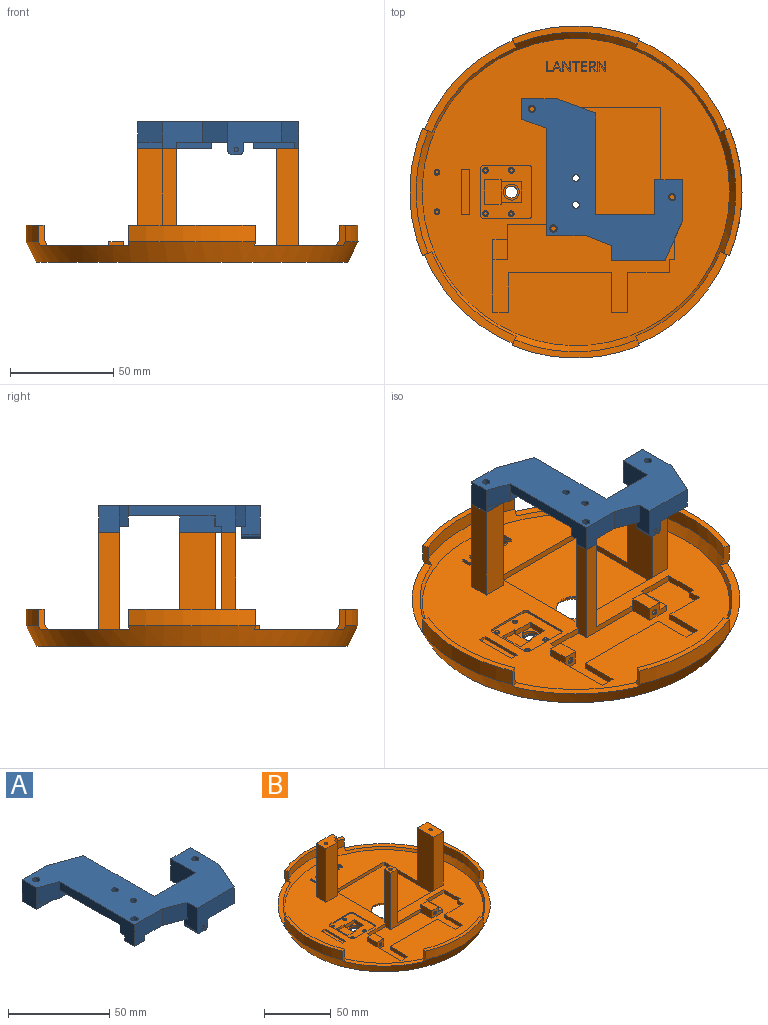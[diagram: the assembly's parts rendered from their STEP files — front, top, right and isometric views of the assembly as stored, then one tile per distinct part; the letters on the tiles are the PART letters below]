
ASSEMBLY  parts=2 mates=1
PART A: 45 faces, bbox 78x78.3x16 mm
  f0: plane 64.21x22mm, normal (0,0,-1), area 784.3mm2, adj f2,f4,f9,f10,f11,f16,f24,f27
  f1: plane 49.3x10mm, normal (1,0,0), area 283.3mm2, adj f2,f18,f23,f33,f35,f36
  f2: plane 28.5x10mm, normal (0,1,0), area 280mm2, adj f0,f1,f24,f33,f35,f38
  f3: plane 2x2mm, normal (0,-1,0), area 3.1mm2, adj f14
  f4: plane 4x3mm, normal (-1,0,0), area 12mm2, adj f0,f9,f10,f17
  f5: plane 3x3mm, normal (1,0,0), area 9mm2, adj f6,f7,f8,f18
  f6: plane 12x3mm, normal (0,-1,0), area 36mm2, adj f5,f7,f18,f21
  f7: plane 36x10mm, normal (0,0,-1), area 210.5mm2, adj f5,f6,f8,f19,f21,f22,f23
  f8: plane 24x3mm, normal (0,-1,0), area 72mm2, adj f5,f7,f18,f23
  f9: plane 8.26x3mm, normal (0,1,0), area 24.8mm2, adj f0,f4,f17,f24
  f10: plane 19.97x3mm, normal (0,-1,0), area 59.9mm2, adj f0,f4,f17,f27
  f11: plane 9x4mm, normal (1,0,0), area 36mm2, adj f0,f12,f16,f28
  f12: cylinder r=2mm len=9mm, axis (0,1,0), area 28.3mm2, adj f11,f13,f16,f28
  f13: plane 9x3.5mm, normal (0,0,-1), area 31.5mm2, adj f12,f15,f16,f28
  f14: cylinder r=1mm len=6mm, axis (0,-1,0), area 37.7mm2, adj f3,f28
  f15: cylinder r=2mm len=9mm, axis (0,-1,0), area 28.3mm2, adj f13,f16,f28,f29
  f16: plane 7.5x6mm, normal (0,1,0), area 43.3mm2, adj f0,f11,f12,f13,f15,f29
  f17: plane 24x21.76mm, normal (0,0,-1), area 343.3mm2, adj f4,f9,f10,f24,f25,f26,f27,f32
  f18: plane 36x7.37mm, normal (0,0,-1), area 203mm2, adj f1,f5,f6,f8,f20,f36
  f19: cylinder r=1.8mm len=13mm, axis (0,0,1), area 147mm2, adj f7,f33
  f20: plane 12x10mm, normal (-0.34,-0.94,0), area 127.7mm2, adj f18,f21,f33,f34,f36
  f21: plane 13x10mm, normal (-1,0,0), area 130mm2, adj f6,f7,f20,f22,f33
  f22: plane 16.77x13mm, normal (0,1,0), area 218mm2, adj f7,f21,f23,f33
  f23: plane 19.23x13mm, normal (0.34,0.94,0), area 266.1mm2, adj f1,f7,f8,f22,f33
  f24: plane 20x13mm, normal (-1,0,0), area 230mm2, adj f0,f2,f9,f17,f25,f33
  f25: plane 13.5x13mm, normal (0,1,0), area 175.5mm2, adj f17,f24,f26,f33
  f26: plane 20x13mm, normal (1,0,0), area 260mm2, adj f17,f25,f27,f33
  f27: plane 19x13mm, normal (0.91,-0.41,0), area 221.3mm2, adj f0,f10,f17,f26,f28,f33
  f28: plane 25.76x16mm, normal (0,-1,0), area 297.8mm2, adj f0,f11,f12,f13,f14,f15,f27,f29
  f29: plane 14x9mm, normal (-1,0,0), area 106mm2, adj f0,f15,f16,f28,f30,f33
  f30: plane 12.39x10mm, normal (-0.36,-0.93,0), area 132.8mm2, adj f0,f29,f31,f33
  f31: plane 19.35x13mm, normal (0,-1,0), area 214.5mm2, adj f0,f30,f33,f34,f39,f41
  f32: cylinder r=1.8mm len=13mm, axis (0,0,1), area 147mm2, adj f17,f33
  f33: plane 78.3x78mm, normal (0,0,1), area 2638.4mm2, adj f1,f2,f19,f20,f21,f22,f23,f24
  f34: plane 52.13x13mm, normal (-1,0,0), area 332.3mm2, adj f0,f20,f31,f33,f35,f37,f40,f41
  f35: plane 42x25mm, normal (0,0,-1), area 991mm2, adj f1,f2,f34,f36,f37,f38,f43,f44
  f36: plane 24x5mm, normal (0,-1,0), area 120mm2, adj f1,f18,f20,f35
  f37: plane 25x5mm, normal (0,1,0), area 125mm2, adj f0,f34,f35,f38
  f38: plane 5x0.07mm, normal (-1,0,0), area 0.3mm2, adj f0,f2,f35,f37
  f39: plane 7x3mm, normal (1,0,0), area 21mm2, adj f0,f31,f40,f41
  f40: plane 7x3mm, normal (0,1,0), area 21mm2, adj f0,f34,f39,f41
  f41: plane 7x7mm, normal (0,0,-1), area 38.8mm2, adj f31,f34,f39,f40,f42
  f42: cylinder r=1.8mm len=13mm, axis (0,0,-1), area 147mm2, adj f33,f41
  f43: cylinder r=1.65mm len=5mm, axis (0,0,1), area 51.8mm2, adj f33,f35
  f44: cylinder r=1.65mm len=5mm, axis (0,0,1), area 51.8mm2, adj f33,f35
PART B: 230 faces, bbox 161x161x55 mm
  f0: cylinder r=80.5mm len=61.61mm, axis (0,0,1), area 505.8mm2, adj f11,f12,f219,f229
  f1: cylinder r=80.5mm len=61.61mm, axis (0,0,1), area 505.8mm2, adj f8,f12,f226,f228
  f2: cylinder r=80.5mm len=61.61mm, axis (0,0,1), area 505.8mm2, adj f9,f12,f223,f225
  f3: cylinder r=80.5mm len=61.61mm, axis (0,0,1), area 505.8mm2, adj f10,f12,f220,f222
  f4: cylinder r=77.5mm len=59.32mm, axis (0,0,-1), area 426.1mm2, adj f8,f13,f226,f228
  f5: cylinder r=77.5mm len=59.32mm, axis (0,0,-1), area 426.1mm2, adj f9,f13,f223,f225
  f6: cylinder r=77.5mm len=59.32mm, axis (0,0,-1), area 426.1mm2, adj f10,f13,f220,f222
  f7: cylinder r=77.5mm len=59.32mm, axis (0,0,-1), area 426.1mm2, adj f11,f13,f219,f229
  f8: plane 61.61x8.9mm, normal (0,0,1), area 186.1mm2, adj f1,f4,f226,f228
  f9: plane 61.61x8.9mm, normal (0,0,1), area 186.1mm2, adj f2,f5,f223,f225
  f10: plane 61.61x8.9mm, normal (0,0,1), area 186.1mm2, adj f3,f6,f220,f222
  f11: plane 61.61x8.9mm, normal (0,0,1), area 186.1mm2, adj f0,f7,f219,f229
  f12: cone r=80.5mm half-angle=26.6deg, axis (0,0,1), area 4917.4mm2, adj f0,f1,f2,f3,f19,f218,f219,f220
  f13: cone r=77.5mm half-angle=31deg, axis (0,0,1), area 1942.5mm2, adj f4,f5,f6,f7,f16,f218,f219,f220
  f14: cylinder r=2.9mm len=5.8mm, axis (0,0,1), area 9.1mm2, adj f19,f217
  f15: plane 26x25mm, normal (0,0,1), area 426.8mm2, adj f171,f172,f173,f174,f175,f176,f177,f178
  f16: plane 149x149mm, normal (0,0,1), area 11513.9mm2, adj f13,f20,f21,f22,f23,f24,f25,f26
  f17: plane 52.5x52.5mm, normal (0,0,1), area 2472.7mm2, adj f18,f39,f40,f41,f43
  f18: cylinder r=9.5mm len=19mm, axis (0,0,1), area 36.8mm2, adj f17,f51
  f19: plane 151x151mm, normal (0,0,-1), area 17466mm2, adj f12,f14,f51
  f20: plane 18.5x3mm, normal (0,-1,0), area 55.5mm2, adj f16,f21,f42,f44
  f21: plane 17x3mm, normal (-1,0,0), area 51mm2, adj f16,f20,f22,f44
  f22: plane 3x2.5mm, normal (0,1,0), area 7.5mm2, adj f16,f21,f23,f44
  f23: plane 6.4x3mm, normal (-1,0,0), area 19.2mm2, adj f16,f22,f24,f44
  f24: plane 20x3mm, normal (0,1,0), area 60mm2, adj f16,f23,f25,f44
  f25: plane 19x3mm, normal (-1,0,0), area 57mm2, adj f16,f24,f26,f44
  f26: plane 8x3mm, normal (0,1,0), area 24mm2, adj f16,f25,f27,f44
  f27: plane 19x3mm, normal (1,0,0), area 57mm2, adj f16,f26,f28,f44
  f28: plane 50x3mm, normal (0,1,0), area 150mm2, adj f16,f27,f29,f44
  f29: plane 19x3mm, normal (-1,0,0), area 57mm2, adj f16,f28,f30,f44
  f30: plane 7.4x3mm, normal (0,1,0), area 22.2mm2, adj f16,f29,f31,f44
  f31: plane 25.4x3mm, normal (1,0,0), area 76.2mm2, adj f16,f30,f32,f44
  f32: plane 7x7mm, normal (0,-1,0), area 41.9mm2, adj f31,f33,f44,f46,f47,f199
  f33: plane 17x7mm, normal (1,0,0), area 91mm2, adj f16,f32,f34,f44,f45,f47
  f34: plane 18.9x3mm, normal (0,-1,0), area 56.7mm2, adj f16,f33,f35,f44
  f35: plane 52x7mm, normal (-1,0,0), area 359.5mm2, adj f16,f34,f36,f44,f200,f202
  f36: plane 52x32mm, normal (0,-1,0), area 439mm2, adj f16,f35,f37,f44,f201,f202
  f37: plane 11.5x7mm, normal (-1,0,0), area 80.5mm2, adj f36,f38,f44,f48,f50
  f38: plane 11.5x7mm, normal (0,-1,0), area 55.4mm2, adj f16,f37,f42,f44,f49,f50,f198
  f39: plane 52.5x52mm, normal (1,0,0), area 304.5mm2, adj f16,f17,f40,f43,f157,f162
  f40: plane 52.5x52mm, normal (0,-1,0), area 244.1mm2, adj f16,f17,f39,f41,f158,f162
  f41: plane 52.5x52mm, normal (-1,0,0), area 1000.3mm2, adj f16,f17,f40,f43,f164,f165,f166
  f42: plane 17x3mm, normal (1,0,0), area 51mm2, adj f16,f20,f38,f44
  f43: plane 52.5x3mm, normal (0,1,0), area 157.5mm2, adj f16,f17,f39,f41
  f44: plane 87.9x42.4mm, normal (0,0,1), area 1843mm2, adj f20,f21,f22,f23,f24,f25,f26,f27
  f45: plane 7x4mm, normal (0,1,0), area 28mm2, adj f16,f33,f46,f47
  f46: plane 10x4mm, normal (-1,0,0), area 40mm2, adj f16,f32,f45,f47
  f47: plane 10x7mm, normal (0,0,1), area 70mm2, adj f32,f33,f45,f46
  f48: plane 7x4mm, normal (0,1,0), area 28mm2, adj f16,f37,f49,f50
  f49: plane 11.5x4mm, normal (1,0,0), area 46mm2, adj f16,f38,f48,f50
  f50: plane 11.5x7mm, normal (0,0,1), area 80.5mm2, adj f37,f38,f48,f49
  f51: cone r=11.5mm half-angle=40deg, axis (0,0,-1), area 205.3mm2, adj f18,f19
  f52: cylinder r=1mm len=4.5mm, axis (0,-1,0), area 28.3mm2, adj f53,f198
  f53: plane 2x2mm, normal (0,-1,0), area 3.1mm2, adj f52
  f54: cylinder r=1mm len=4.5mm, axis (0,-1,0), area 28.3mm2, adj f55,f199
  f55: plane 2x2mm, normal (0,-1,0), area 3.1mm2, adj f54
  f56: cylinder r=0.88mm len=3.5mm, axis (0,0,1), area 19.2mm2, adj f57,f196
  f57: plane 1.75x1.75mm, normal (0,0,1), area 2.4mm2, adj f56
  f58: cylinder r=0.88mm len=3.5mm, axis (0,0,1), area 19.2mm2, adj f59,f197
  f59: plane 1.75x1.75mm, normal (0,0,1), area 2.4mm2, adj f58
  f60: plane 4.92x1mm, normal (-1,0,0), area 4.9mm2, adj f16,f61,f65,f66
  f61: plane 2.74x1mm, normal (0,-1,0), area 2.7mm2, adj f16,f60,f62,f66
  f62: plane 1x0.52mm, normal (1,0,0), area 0.5mm2, adj f16,f61,f63,f66
  f63: plane 2.17x1mm, normal (0,1,0), area 2.2mm2, adj f16,f62,f64,f66
  f64: plane 4.4x1mm, normal (1,0,0), area 4.4mm2, adj f16,f63,f65,f66
  f65: plane 1x0.57mm, normal (0,1,0), area 0.6mm2, adj f16,f60,f64,f66
  f66: plane 4.92x2.74mm, normal (0,0,1), area 3.9mm2, adj f60,f61,f62,f63,f64,f65
  f67: plane 1.52x1mm, normal (-0.94,-0.35,0), area 1.6mm2, adj f68,f79,f80,f81
  f68: plane 1.59x1mm, normal (0,1,0), area 1.6mm2, adj f67,f69,f80,f81
  f69: plane 1.52x1mm, normal (0.94,-0.35,0), area 1.6mm2, adj f68,f70,f80,f81
  f70: extruded ~1x0.71mm, area 0.7mm2, adj f69,f79,f80,f81
  f71: plane 1.56x1mm, normal (-0.93,-0.36,0), area 1.7mm2, adj f16,f72,f78,f80
  f72: plane 1x0.59mm, normal (0,-1,0), area 0.6mm2, adj f16,f71,f73,f80
  f73: plane 4.94x1.93mm, normal (0.93,0.36,0), area 5.3mm2, adj f16,f72,f74,f80
  f74: plane 1x0.48mm, normal (0,1,0), area 0.5mm2, adj f16,f73,f75,f80
  f75: plane 4.94x1.94mm, normal (-0.93,0.37,0), area 5.3mm2, adj f16,f74,f76,f80
  f76: plane 1x0.58mm, normal (0,-1,0), area 0.6mm2, adj f16,f75,f77,f80
  f77: plane 1.56x1mm, normal (0.93,-0.36,0), area 1.7mm2, adj f16,f76,f78,f80
  f78: plane 1.97x1mm, normal (0,-1,0), area 2mm2, adj f16,f71,f77,f80
  f79: extruded ~1x0.71mm, area 0.7mm2, adj f67,f70,f80,f81
  f80: plane 4.94x4.36mm, normal (0,0,1), area 6.2mm2, adj f67,f68,f69,f70,f71,f72,f73,f74
  f81: plane 2.23x1.59mm, normal (0,0,1), area 1.7mm2, adj f67,f68,f69,f70,f79
  f82: plane 1x0.65mm, normal (0,-1,0), area 0.7mm2, adj f16,f83,f96,f97
  f83: plane 4.92x1mm, normal (1,0,0), area 4.9mm2, adj f16,f82,f84,f97
  f84: plane 1x0.54mm, normal (0,1,0), area 0.5mm2, adj f16,f83,f85,f97
  f85: plane 2.82x1mm, normal (-1,0,0), area 2.8mm2, adj f16,f84,f86,f97
  f86: extruded ~1x0.71mm, area 0.7mm2, adj f16,f85,f87,f97
  f87: extruded ~1x0.58mm, area 0.6mm2, adj f16,f86,f88,f97
  f88: plane 1x0.03mm, normal (0,1,0), area 0mm2, adj f16,f87,f89,f97
  f89: plane 4.11x2.68mm, normal (0.84,0.55,0), area 4.9mm2, adj f16,f88,f90,f97
  f90: plane 1x0.65mm, normal (0,1,0), area 0.6mm2, adj f16,f89,f91,f97
  f91: plane 4.92x1mm, normal (-1,0,0), area 4.9mm2, adj f16,f90,f92,f97
  f92: plane 1x0.53mm, normal (0,-1,0), area 0.5mm2, adj f16,f91,f93,f97
  f93: plane 2.8x1mm, normal (1,0,0), area 2.8mm2, adj f16,f92,f94,f97
  f94: extruded ~1.33x1mm, area 1.3mm2, adj f16,f93,f95,f97
  f95: plane 1x0.03mm, normal (0,-1,0), area 0mm2, adj f16,f94,f96,f97
  f96: plane 4.13x2.69mm, normal (-0.84,-0.55,0), area 4.9mm2, adj f16,f82,f95,f97
  f97: plane 4.92x3.84mm, normal (0,0,1), area 8mm2, adj f82,f83,f84,f85,f86,f87,f88,f89
  f98: plane 1x0.57mm, normal (0,-1,0), area 0.6mm2, adj f16,f99,f105,f106
  f99: plane 4.41x1mm, normal (1,0,0), area 4.4mm2, adj f16,f98,f100,f106
  f100: plane 1.56x1mm, normal (0,-1,0), area 1.6mm2, adj f16,f99,f101,f106
  f101: plane 1x0.51mm, normal (1,0,0), area 0.5mm2, adj f16,f100,f102,f106
  f102: plane 3.69x1mm, normal (0,1,0), area 3.7mm2, adj f16,f101,f103,f106
  f103: plane 1x0.51mm, normal (-1,0,0), area 0.5mm2, adj f16,f102,f104,f106
  f104: plane 1.56x1mm, normal (0,-1,0), area 1.6mm2, adj f16,f103,f105,f106
  f105: plane 4.41x1mm, normal (-1,0,0), area 4.4mm2, adj f16,f98,f104,f106
  f106: plane 4.92x3.69mm, normal (0,0,1), area 4.4mm2, adj f98,f99,f100,f101,f102,f103,f104,f105
  f107: plane 2.74x1mm, normal (0,-1,0), area 2.7mm2, adj f16,f108,f118,f119
  f108: plane 1x0.51mm, normal (1,0,0), area 0.5mm2, adj f16,f107,f109,f119
  f109: plane 2.17x1mm, normal (0,1,0), area 2.2mm2, adj f16,f108,f110,f119
  f110: plane 1.81x1mm, normal (1,0,0), area 1.8mm2, adj f16,f109,f111,f119
  f111: plane 2.04x1mm, normal (0,-1,0), area 2mm2, adj f16,f110,f112,f119
  f112: plane 1x0.51mm, normal (1,0,0), area 0.5mm2, adj f16,f111,f113,f119
  f113: plane 2.04x1mm, normal (0,1,0), area 2mm2, adj f16,f112,f114,f119
  f114: plane 1.58x1mm, normal (1,0,0), area 1.6mm2, adj f16,f113,f115,f119
  f115: plane 2.17x1mm, normal (0,-1,0), area 2.2mm2, adj f16,f114,f116,f119
  f116: plane 1x0.51mm, normal (1,0,0), area 0.5mm2, adj f16,f115,f117,f119
  f117: plane 2.74x1mm, normal (0,1,0), area 2.7mm2, adj f16,f116,f118,f119
  f118: plane 4.92x1mm, normal (-1,0,0), area 4.9mm2, adj f16,f107,f117,f119
  f119: plane 4.92x2.74mm, normal (0,0,1), area 6.1mm2, adj f107,f108,f109,f110,f111,f112,f113,f114
  f120: plane 1x0.79mm, normal (0,1,0), area 0.8mm2, adj f121,f137,f138,f139
  f121: plane 1.88x1mm, normal (1,0,0), area 1.9mm2, adj f120,f122,f138,f139
  f122: plane 1x0.74mm, normal (0,-1,0), area 0.7mm2, adj f121,f123,f138,f139
  f123: extruded ~1x0.92mm, area 1mm2, adj f122,f124,f138,f139
  f124: extruded ~1x0.7mm, area 0.8mm2, adj f123,f125,f138,f139
  f125: extruded ~1x0.72mm, area 0.8mm2, adj f124,f137,f138,f139
  f126: plane 2.05x1mm, normal (1,0,0), area 2mm2, adj f16,f127,f136,f138
  f127: plane 1.03x1mm, normal (0,-1,0), area 1mm2, adj f16,f126,f128,f138
  f128: plane 2.05x1.19mm, normal (-0.86,-0.5,0), area 2.4mm2, adj f16,f127,f129,f138
  f129: plane 1x0.68mm, normal (0,-1,0), area 0.7mm2, adj f16,f128,f130,f138
  f130: plane 2.21x1.34mm, normal (0.86,0.52,0), area 2.6mm2, adj f16,f129,f131,f138
  f131: extruded ~1.32x1mm, area 1.8mm2, adj f16,f130,f132,f138
  f132: extruded ~1.04x1mm, area 1.2mm2, adj f16,f131,f133,f138
  f133: extruded ~1.34x1mm, area 1.4mm2, adj f16,f132,f134,f138
  f134: plane 1.35x1mm, normal (0,1,0), area 1.3mm2, adj f16,f133,f135,f138
  f135: plane 4.92x1mm, normal (-1,0,0), area 4.9mm2, adj f16,f134,f136,f138
  f136: plane 1x0.57mm, normal (0,-1,0), area 0.6mm2, adj f16,f126,f135,f138
  f137: extruded ~1x0.89mm, area 0.9mm2, adj f120,f125,f138,f139
  f138: plane 4.92x3.47mm, normal (0,0,1), area 7.3mm2, adj f120,f121,f122,f123,f124,f125,f126,f127
  f139: plane 1.96x1.88mm, normal (0,0,1), area 3.3mm2, adj f120,f121,f122,f123,f124,f125,f137
  f140: plane 1x0.65mm, normal (0,-1,0), area 0.7mm2, adj f16,f141,f154,f155
  f141: plane 4.92x1mm, normal (1,0,0), area 4.9mm2, adj f16,f140,f142,f155
  f142: plane 1x0.54mm, normal (0,1,0), area 0.5mm2, adj f16,f141,f143,f155
  f143: plane 2.82x1mm, normal (-1,0,0), area 2.8mm2, adj f16,f142,f144,f155
  f144: extruded ~1x0.71mm, area 0.7mm2, adj f16,f143,f145,f155
  f145: extruded ~1x0.58mm, area 0.6mm2, adj f16,f144,f146,f155
  f146: plane 1x0.03mm, normal (0,1,0), area 0mm2, adj f16,f145,f147,f155
  f147: plane 4.11x2.68mm, normal (0.84,0.55,0), area 4.9mm2, adj f16,f146,f148,f155
  f148: plane 1x0.65mm, normal (0,1,0), area 0.6mm2, adj f16,f147,f149,f155
  f149: plane 4.92x1mm, normal (-1,0,0), area 4.9mm2, adj f16,f148,f150,f155
  f150: plane 1x0.53mm, normal (0,-1,0), area 0.5mm2, adj f16,f149,f151,f155
  f151: plane 2.8x1mm, normal (1,0,0), area 2.8mm2, adj f16,f150,f152,f155
  f152: extruded ~1.33x1mm, area 1.3mm2, adj f16,f151,f153,f155
  f153: plane 1x0.03mm, normal (0,-1,0), area 0mm2, adj f16,f152,f154,f155
  f154: plane 4.13x2.69mm, normal (-0.84,-0.55,0), area 4.9mm2, adj f16,f140,f153,f155
  f155: plane 4.92x3.84mm, normal (0,0,1), area 8mm2, adj f140,f141,f142,f143,f144,f145,f146,f147
  f156: plane 49x3mm, normal (1,0,0), area 147mm2, adj f16,f157,f161,f162
  f157: plane 49x3mm, normal (0,-1,0), area 147mm2, adj f16,f39,f156,f162
  f158: plane 49x4mm, normal (1,0,0), area 196mm2, adj f16,f40,f159,f162
  f159: plane 49x16.77mm, normal (0,1,0), area 821.6mm2, adj f16,f158,f160,f162
  f160: plane 49x10mm, normal (-1,0,0), area 490mm2, adj f16,f159,f161,f162
  f161: plane 49x12mm, normal (0,-1,0), area 588mm2, adj f16,f156,f160,f162
  f162: plane 16.77x10mm, normal (0,0,1), area 142.8mm2, adj f39,f40,f156,f157,f158,f159,f160,f161
  f163: plane 49x17.2mm, normal (1,0,0), area 842.8mm2, adj f16,f164,f165,f166
  f164: plane 49x10.5mm, normal (0,1,0), area 514.5mm2, adj f16,f41,f163,f166
  f165: plane 49x10.5mm, normal (0,-1,0), area 514.5mm2, adj f16,f41,f163,f166
  f166: plane 17.2x10.5mm, normal (0,0,1), area 175.3mm2, adj f41,f163,f164,f165,f169
  f167: cylinder r=1.3mm len=20mm, axis (0,0,1), area 163.4mm2, adj f162,f168
  f168: plane 2.6x2.6mm, normal (0,0,1), area 5.3mm2, adj f167
  f169: cylinder r=1.3mm len=20mm, axis (0,0,1), area 163.4mm2, adj f166,f170
  f170: plane 2.6x2.6mm, normal (0,0,1), area 5.3mm2, adj f169
  f171: plane 21x1mm, normal (0,-1,0), area 21mm2, adj f15,f16,f172,f178
  f172: cylinder r=2mm len=2mm, axis (0,0,1), area 3.1mm2, adj f15,f16,f171,f173
  f173: plane 22x1mm, normal (1,0,0), area 22mm2, adj f15,f16,f172,f174
  f174: cylinder r=2mm len=2mm, axis (0,0,1), area 3.1mm2, adj f15,f16,f173,f175
  f175: plane 21x1mm, normal (0,1,0), area 21mm2, adj f15,f16,f174,f176
  f176: cylinder r=2mm len=2mm, axis (0,0,1), area 3.1mm2, adj f15,f16,f175,f177
  f177: plane 22x1mm, normal (-1,0,0), area 22mm2, adj f15,f16,f176,f178
  f178: cylinder r=2mm len=2mm, axis (0,0,1), area 3.1mm2, adj f15,f16,f171,f177
  f179: cylinder r=0.88mm len=3.5mm, axis (0,0,1), area 19.2mm2, adj f180,f194
  f180: plane 1.75x1.75mm, normal (0,0,1), area 2.4mm2, adj f179
  f181: cylinder r=0.88mm len=3.5mm, axis (0,0,1), area 19.2mm2, adj f182,f195
  f182: plane 1.75x1.75mm, normal (0,0,1), area 2.4mm2, adj f181
  f183: cylinder r=0.88mm len=3.5mm, axis (0,0,1), area 19.2mm2, adj f184,f192
  f184: plane 1.75x1.75mm, normal (0,0,1), area 2.4mm2, adj f183
  f185: cylinder r=0.88mm len=3.5mm, axis (0,0,1), area 19.2mm2, adj f186,f193
  f186: plane 1.75x1.75mm, normal (0,0,1), area 2.4mm2, adj f185
  f187: plane 10x3mm, normal (0,-1,0), area 30mm2, adj f15,f188,f190,f191,f210
  f188: plane 10x1mm, normal (1,0,0), area 10mm2, adj f187,f189,f191,f215
  f189: plane 10x3mm, normal (0,1,0), area 30mm2, adj f15,f188,f190,f191,f211
  f190: plane 10x3mm, normal (-1,0,0), area 30mm2, adj f15,f187,f189,f191
  f191: plane 10x10mm, normal (0,0,1), area 52.8mm2, adj f187,f188,f189,f190,f216
  f192: cone r=0.88mm half-angle=45deg, axis (0,0,1), area 5mm2, adj f15,f183
  f193: cone r=0.88mm half-angle=45deg, axis (0,0,1), area 5mm2, adj f15,f185
  f194: cone r=0.88mm half-angle=45deg, axis (0,0,1), area 5mm2, adj f15,f179
  f195: cone r=0.88mm half-angle=45deg, axis (0,0,1), area 5mm2, adj f15,f181
  f196: cone r=0.88mm half-angle=45deg, axis (0,0,1), area 5mm2, adj f16,f56
  f197: cone r=0.88mm half-angle=45deg, axis (0,0,1), area 5mm2, adj f16,f58
  f198: cone r=1mm half-angle=45deg, axis (0,-1,0), area 5.6mm2, adj f38,f52
  f199: cone r=1mm half-angle=45deg, axis (0,-1,0), area 5.6mm2, adj f32,f54
  f200: plane 49x7mm, normal (0,1,0), area 343mm2, adj f16,f35,f201,f202
  f201: plane 49x7mm, normal (1,0,0), area 343mm2, adj f16,f36,f200,f202
  f202: plane 7x7mm, normal (0,0,1), area 43.7mm2, adj f35,f36,f200,f201,f203
  f203: cylinder r=1.3mm len=20mm, axis (0,0,1), area 163.4mm2, adj f202,f204
  f204: plane 2.6x2.6mm, normal (0,0,1), area 5.3mm2, adj f203
  f205: plane 4x1.5mm, normal (0,-1,0), area 6mm2, adj f16,f206,f208,f209
  f206: plane 22x1.5mm, normal (1,0,0), area 33mm2, adj f16,f205,f207,f209
  f207: plane 4x1.5mm, normal (0,1,0), area 6mm2, adj f16,f206,f208,f209
  f208: plane 22x1.5mm, normal (-1,0,0), area 33mm2, adj f16,f205,f207,f209
  f209: plane 22x4mm, normal (0,0,1), area 88mm2, adj f205,f206,f207,f208
  f210: plane 2x1mm, normal (-1,0,0), area 2mm2, adj f15,f187,f212,f215
  f211: plane 2x1mm, normal (-1,0,0), area 2mm2, adj f15,f189,f214,f215
  f212: plane 8x2mm, normal (0,-1,0), area 16mm2, adj f15,f210,f213,f215
  f213: plane 12x2mm, normal (1,0,0), area 24mm2, adj f15,f212,f214,f215
  f214: plane 8x2mm, normal (0,1,0), area 16mm2, adj f15,f211,f213,f215
  f215: plane 12x8mm, normal (0,0,1), area 96mm2, adj f188,f210,f211,f212,f213,f214
  f216: cylinder r=3.88mm len=7.75mm, axis (0,0,1), area 36.5mm2, adj f191,f217
  f217: plane 7.75x7.75mm, normal (0,0,1), area 20.8mm2, adj f14,f216
  f218: plane 44.48x44.48mm, normal (0,0,1), area 231.6mm2, adj f12,f13,f219,f220
  f219: plane 10x4.43mm, normal (0.38,0.92,0), area 31.7mm2, adj f0,f7,f11,f12,f13,f218
  f220: plane 10x4.43mm, normal (-0.92,-0.38,0), area 31.7mm2, adj f3,f6,f10,f12,f13,f218
  f221: plane 44.48x44.48mm, normal (0,0,1), area 231.6mm2, adj f12,f13,f222,f223
  f222: plane 10x4.43mm, normal (0.92,-0.38,0), area 31.7mm2, adj f3,f6,f10,f12,f13,f221
  f223: plane 10x4.43mm, normal (-0.38,0.92,0), area 31.7mm2, adj f2,f5,f9,f12,f13,f221
  f224: plane 44.48x44.48mm, normal (0,0,1), area 231.6mm2, adj f12,f13,f225,f226
  f225: plane 10x4.43mm, normal (-0.38,-0.92,0), area 31.7mm2, adj f2,f5,f9,f12,f13,f224
  f226: plane 10x4.43mm, normal (0.92,0.38,0), area 31.7mm2, adj f1,f4,f8,f12,f13,f224
  f227: plane 44.48x44.48mm, normal (0,0,1), area 231.6mm2, adj f12,f13,f228,f229
  f228: plane 10x4.43mm, normal (-0.92,0.38,0), area 31.7mm2, adj f1,f4,f8,f12,f13,f227
  f229: plane 10x4.43mm, normal (0.38,-0.92,0), area 31.7mm2, adj f0,f7,f11,f12,f13,f227
PLACE A t=(-13.9,-3.89,59.7)mm
PLACE B t=(-13.9,-4.09,4.5)mm
MATE parallel A.f7 <-> B.f162  axis (0,0,1) through (-23.44,41.11,56.7)mm
